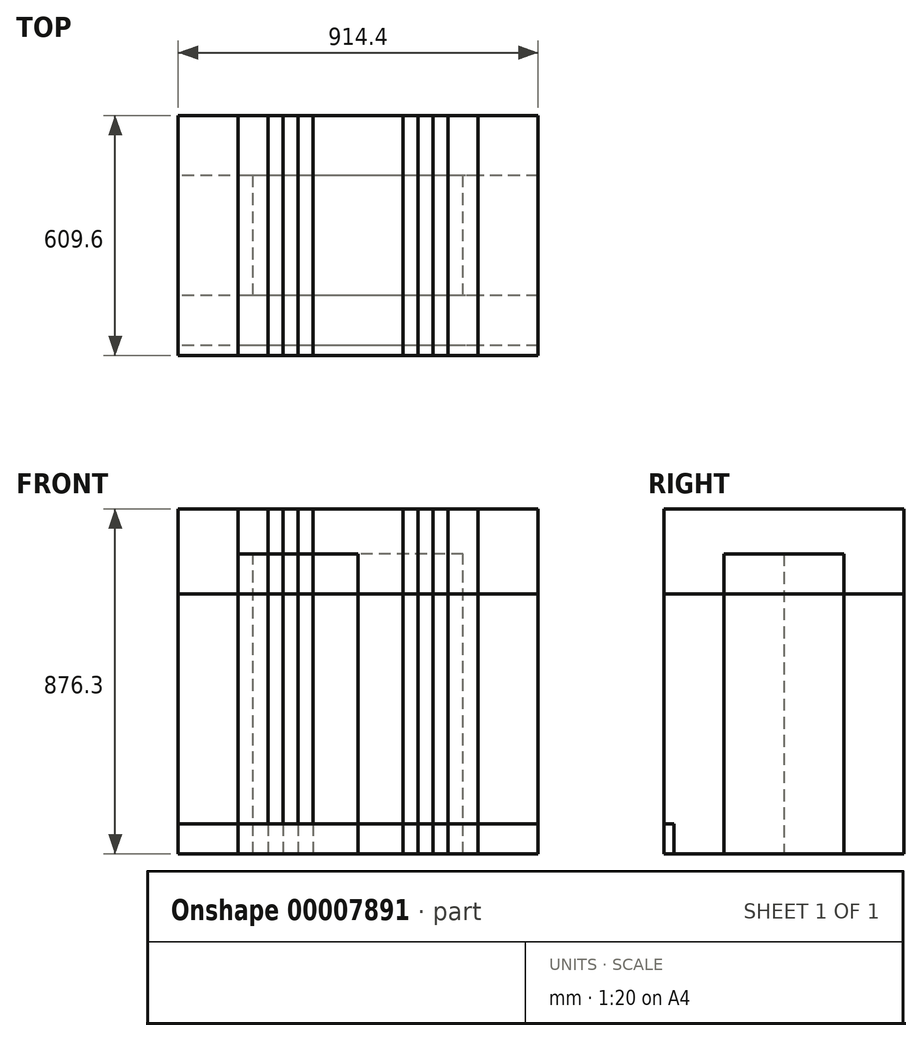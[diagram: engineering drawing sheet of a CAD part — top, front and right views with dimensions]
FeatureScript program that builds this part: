
annotation { "Feature Type Name" : "Feature", "Feature Type Description" : "" }
export const myFeature = defineFeature(function(context is Context, id is Id, definition is map)
    precondition{}
    {
        {
            var Q0;
            Q0=qCreatedBy(makeId("Right.planeOp"),FACE);
            var sketch = newSketch(context, id + "F0", { "sketchPlane" : qUnion([Q0])});
            skLineSegment(sketch, "E0", {"start": v(304.8, 0) * mm, "end": v(304.8, 876.3) * mm});
            skLineSegment(sketch, "E1", {"start": v(304.8, 876.3) * mm, "end": v(-304.8, 876.3) * mm});
            skLineSegment(sketch, "E2", {"start": v(-304.8, 876.3) * mm, "end": v(-304.8, 76.2) * mm});
            skLineSegment(sketch, "E3", {"start": v(-304.8, 76.2) * mm, "end": v(-279.4, 76.2) * mm});
            skLineSegment(sketch, "E4", {"start": v(-279.4, 76.2) * mm, "end": v(-279.4, 0) * mm});
            skLineSegment(sketch, "E5", {"start": v(-279.4, 0) * mm, "end": v(304.8, 0) * mm});
            skPoint(sketch, "E6", {"position": v(0, 876.3) * mm});
            skSolve(sketch);
        }
        {
            var Q0;
            Q0=makeQuery(id+"F0.imprint","IMPRINT",FACE,{"disambiguationData":[TD([[makeQuery(id+"F0.imprint","IMPRINT",EDGE,{"derivedFrom":sQuery(id+"F0.wireOp",EDGE,"E0")}),1.0]])]});
            extrude(context, id + "F1", {"entities" : qUnion([Q0]), "depth" : 914.4 * mm, "offsetDistance" : 25.4 * mm, "symmetric" : true});
        }
        {
            var Q0;
            Q0 = qSketchRegion(id + "F0", true);
            extrude(context, id + "F2", {"entities" : qUnion([Q0]), "depth" : 609.6 * mm, "offsetDistance" : 25.4 * mm, "symmetric" : true});
        }
        {
            var Q0;
            Q0 = qSketchRegion(id + "F0", true);
            extrude(context, id + "F3", {"entities" : qUnion([Q0]), "depth" : 457.2 * mm, "offsetDistance" : 25.4 * mm, "symmetric" : true});
        }
        {
            var Q0;
            Q0 = qSketchRegion(id + "F0", true);
            extrude(context, id + "F4", {"entities" : qUnion([Q0]), "depth" : 381 * mm, "offsetDistance" : 25.4 * mm, "symmetric" : true});
        }
        {
            var Q0;
            Q0 = qSketchRegion(id + "F0", true);
            extrude(context, id + "F5", {"entities" : qUnion([Q0]), "depth" : 304.8 * mm, "offsetDistance" : 25.4 * mm, "symmetric" : true});
        }
        {
            var Q0;
            Q0 = qSketchRegion(id + "F0", true);
            extrude(context, id + "F6", {"entities" : qUnion([Q0]), "depth" : 228.6 * mm, "offsetDistance" : 25.4 * mm, "symmetric" : true});
        }
        {
            var Q0;
            Q0=qCreatedBy(makeId("Right.planeOp"),FACE);
            var sketch = newSketch(context, id + "F7", { "sketchPlane" : qUnion([Q0])});
            skLineSegment(sketch, "E7", {"start": v(304.8, 0) * mm, "end": v(-279.4, 0) * mm});
            skLineSegment(sketch, "E8", {"start": v(-279.4, 0) * mm, "end": v(-279.4, 76.2) * mm});
            skLineSegment(sketch, "E9", {"start": v(-279.4, 76.2) * mm, "end": v(-304.8, 76.2) * mm});
            skLineSegment(sketch, "E10", {"start": v(-304.8, 76.2) * mm, "end": v(-304.8, 660.4) * mm});
            skLineSegment(sketch, "E11", {"start": v(-304.8, 660.4) * mm, "end": v(304.8, 660.4) * mm});
            skLineSegment(sketch, "E12", {"start": v(304.8, 660.4) * mm, "end": v(304.8, 0) * mm});
            skPoint(sketch, "E13", {"position": v(0, 660.4) * mm});
            skSolve(sketch);
        }
        {
            var Q0;
            Q0 = qSketchRegion(id + "F7", true);
            extrude(context, id + "F8", {"entities" : qUnion([Q0]), "depth" : 914.4 * mm, "offsetDistance" : 25.4 * mm, "symmetric" : true});
        }
        {
            var Q0;
            Q0=qCreatedBy(makeId("Right.planeOp"),FACE);
            var sketch = newSketch(context, id + "F9", { "sketchPlane" : qUnion([Q0])});
            skLineSegment(sketch, "E14.bottom", {"start": v(-152.4, 0) * mm, "end": v(152.4, 0) * mm});
            skLineSegment(sketch, "E14.top", {"start": v(-152.4, 762) * mm, "end": v(152.4, 762) * mm});
            skLineSegment(sketch, "E14.left", {"start": v(-152.4, 0) * mm, "end": v(-152.4, 762) * mm});
            skLineSegment(sketch, "E14.right", {"start": v(152.4, 0) * mm, "end": v(152.4, 762) * mm});
            skSolve(sketch);
        }
        {
            var Q0;
            Q0 = qSketchRegion(id + "F9", true);
            extrude(context, id + "F10", {"entities" : qUnion([Q0]), "depth" : 914.4 * mm, "offsetDistance" : 25.4 * mm, "symmetric" : true});
        }
        {
            var Q0;
            Q0 = qSketchRegion(id + "F9", true);
            extrude(context, id + "F11", {"entities" : qUnion([Q0]), "depth" : 609.6 * mm, "offsetDistance" : 25.4 * mm, "symmetric" : true});
        }
        {
            var Q0;
            Q0 = qSketchRegion(id + "F9", true);
            extrude(context, id + "F12", {"entities" : qUnion([Q0]), "depth" : 533.4 * mm, "offsetDistance" : 25.4 * mm, "symmetric" : true});
        }
        {
            var Q0;
            Q0 = qSketchRegion(id + "F9", true);
            extrude(context, id + "F13", {"entities" : qUnion([Q0]), "depth" : 457.2 * mm, "offsetDistance" : 25.4 * mm, "symmetric" : true});
        }
        {
            var Q0;
            Q0 = qSketchRegion(id + "F9", true);
            extrude(context, id + "F14", {"entities" : qUnion([Q0]), "depth" : 381 * mm, "offsetDistance" : 25.4 * mm, "symmetric" : true});
        }
        {
            var Q0;
            Q0 = qSketchRegion(id + "F9", true);
            extrude(context, id + "F15", {"entities" : qUnion([Q0]), "depth" : 304.8 * mm, "offsetDistance" : 25.4 * mm, "symmetric" : true});
        }
        {
            var Q0;
            Q0 = qSketchRegion(id + "F9", true);
            extrude(context, id + "F16", {"entities" : qUnion([Q0]), "depth" : 228.6 * mm, "offsetDistance" : 25.4 * mm, "symmetric" : true});
        }
        {
            var Q0;
            Q0=qCreatedBy(makeId("Top.planeOp"),FACE);
            var sketch = newSketch(context, id + "F17", { "sketchPlane" : qUnion([Q0])});
            skLineSegment(sketch, "E15", {"start": v(304.8, 0) * mm, "end": v(0, -304.8) * mm});
            skLineSegment(sketch, "E16", {"start": v(0, -304.8) * mm, "end": v(-304.8, -304.8) * mm});
            skLineSegment(sketch, "E17", {"start": v(-304.8, -304.8) * mm, "end": v(-304.8, 304.8) * mm});
            skLineSegment(sketch, "E18", {"start": v(-304.8, 304.8) * mm, "end": v(304.8, 304.8) * mm});
            skLineSegment(sketch, "E19", {"start": v(304.8, 304.8) * mm, "end": v(304.8, 0) * mm});
            skSolve(sketch);
        }
        {
            var Q0;
            Q0 = qSketchRegion(id + "F17", true);
            extrude(context, id + "F18", {"entities" : qUnion([Q0]), "depth" : 762 * mm, "offsetDistance" : 25.4 * mm});
        }
    });
